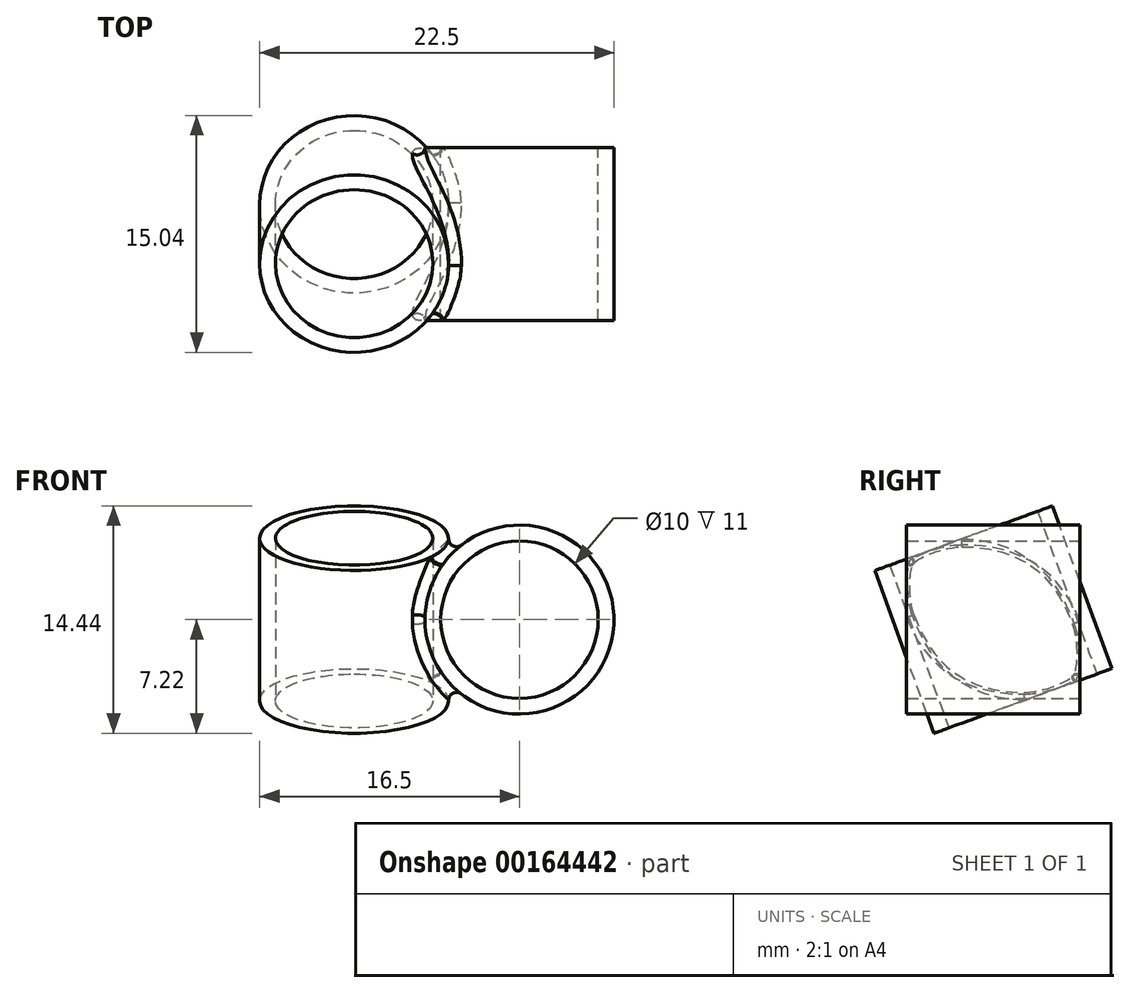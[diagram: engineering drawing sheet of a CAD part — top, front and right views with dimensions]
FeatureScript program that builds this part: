
annotation { "Feature Type Name" : "Feature", "Feature Type Description" : "" }
export const myFeature = defineFeature(function(context is Context, id is Id, definition is map)
    precondition{}
    {
        {
            assignVariable(context, id + "F0", {"name" : "diameter", "anyValue" : 10});
        }
        {
            var Q0;
            Q0=qCreatedBy(makeId("Front.planeOp"),FACE);
            var sketch = newSketch(context, id + "F1", { "sketchPlane" : qUnion([Q0])});
            skCircle(sketch, "E0", {"center": v(0, 0) * mm, "radius": 5 * mm});
            skCircle(sketch, "E1.0", {"center": v(0, 0) * mm, "radius": 6 * mm});
            skLineSegment(sketch, "E2", {"start": v(0, 0) * mm, "end": v(5, 0) * mm, "construction": true});
            skSolve(sketch);
        }
        {
            var Q0;
            Q0=qSketchRegion(id+"F1",true);
            var Q1;
            Q1=makeQuery(id+"F1.imprint","IMPRINT",FACE,{"disambiguationData":[TD([[makeQuery(id+"F1.imprint","IMPRINT",EDGE,{"derivedFrom":sQuery(id+"F1.wireOp",EDGE,"E0")}),1.0]])]});
            extrude(context, id + "F2", {"entities" : qUnion([Q0, Q1]), "endBound" : BoundingType.SYMMETRIC, "oppositeDirection" : true, "depth" : (getVariable(context, 'diameter') + 1) * mm});
        }
        {
            var Q0;
            Q0=sQuery(id+"F1.wireOp",EDGE,"E2");
            var Q1;
            Q1=qCreatedBy(makeId("Front.planeOp"),FACE);
            cPlane(context, id + "F3", {"entities" : qUnion([Q0, Q1]), "cplaneType" : CPlaneType.LINE_ANGLE, "offset" : 25 * mm, "angle" : 290 * degree, "width" : 150 * mm, "height" : 150 * mm});
        }
        {
            var Q0;
            Q0=qCreatedBy(id+"F3.planeOp",FACE);
            var sketch = newSketch(context, id + "F4", { "sketchPlane" : qUnion([Q0])});
            skCircle(sketch, "E3", {"center": v(-10.5, 0) * mm, "radius": 5 * mm});
            skCircle(sketch, "E4.0", {"center": v(-10.5, 0) * mm, "radius": 6 * mm});
            skSolve(sketch);
        }
        {
            var Q0;
            Q0=makeQuery(id+"F4.imprint","IMPRINT",FACE,{"disambiguationData":[TD([[makeQuery(id+"F4.imprint","IMPRINT",EDGE,{"derivedFrom":sQuery(id+"F4.wireOp",EDGE,"E3")}),1.0]])]});
            var Q1;
            Q1=makeQuery(id+"F4.imprint","IMPRINT",FACE,{"disambiguationData":[TD([[makeQuery(id+"F4.imprint","IMPRINT",EDGE,{"derivedFrom":sQuery(id+"F4.wireOp",EDGE,"E3")}),-1.0]])]});
            extrude(context, id + "F5", {"entities" : qUnion([Q0, Q1]), "operationType" : NewBodyOperationType.ADD, "endBound" : BoundingType.SYMMETRIC, "depth" : (getVariable(context, 'diameter') + 1) * mm});
        }
        {
            var Q0;
            Q0=makeQuery(id+"F1.imprint","IMPRINT",FACE,{"disambiguationData":[TD([[makeQuery(id+"F1.imprint","IMPRINT",EDGE,{"derivedFrom":sQuery(id+"F1.wireOp",EDGE,"E0")}),1.0]])]});
            extrude(context, id + "F6", {"entities" : qUnion([Q0]), "operationType" : NewBodyOperationType.REMOVE, "endBound" : BoundingType.THROUGH_ALL, "depth" : 50 * mm, "hasSecondDirection" : true, "secondDirectionOppositeDirection" : true, "secondDirectionDepth" : 32.5 * mm});
        }
        {
            var Q0;
            Q0=makeQuery(id+"F4.imprint","IMPRINT",FACE,{"disambiguationData":[TD([[makeQuery(id+"F4.imprint","IMPRINT",EDGE,{"derivedFrom":sQuery(id+"F4.wireOp",EDGE,"E3")}),1.0]])]});
            extrude(context, id + "F7", {"entities" : qUnion([Q0]), "operationType" : NewBodyOperationType.REMOVE, "endBound" : BoundingType.SYMMETRIC, "oppositeDirection" : true, "depth" : 50 * mm});
        }
        {
            var Q0;
            Q0=makeQuery(id+"F5.boolean.opBoolean","INTERSECT",EDGE,{"derivedFrom":[makeQuery(id+"F2.opExtrude","SWEPT_FACE",FACE,{"disambiguationData":[OSD([sQuery(id+"F1.wireOp",EDGE,"E1.0")])]}),makeQuery(id+"F5.opExtrude","SWEPT_FACE",FACE,{"disambiguationData":[OSD([sQuery(id+"F4.wireOp",EDGE,"E4.0")])]})]});
            fillet(context, id + "F8", {"entities" : qUnion([Q0]), "radius" : 0.5 * mm, "tangentPropagation" : true, "allowEdgeOverflow" : false});
        }
    });
